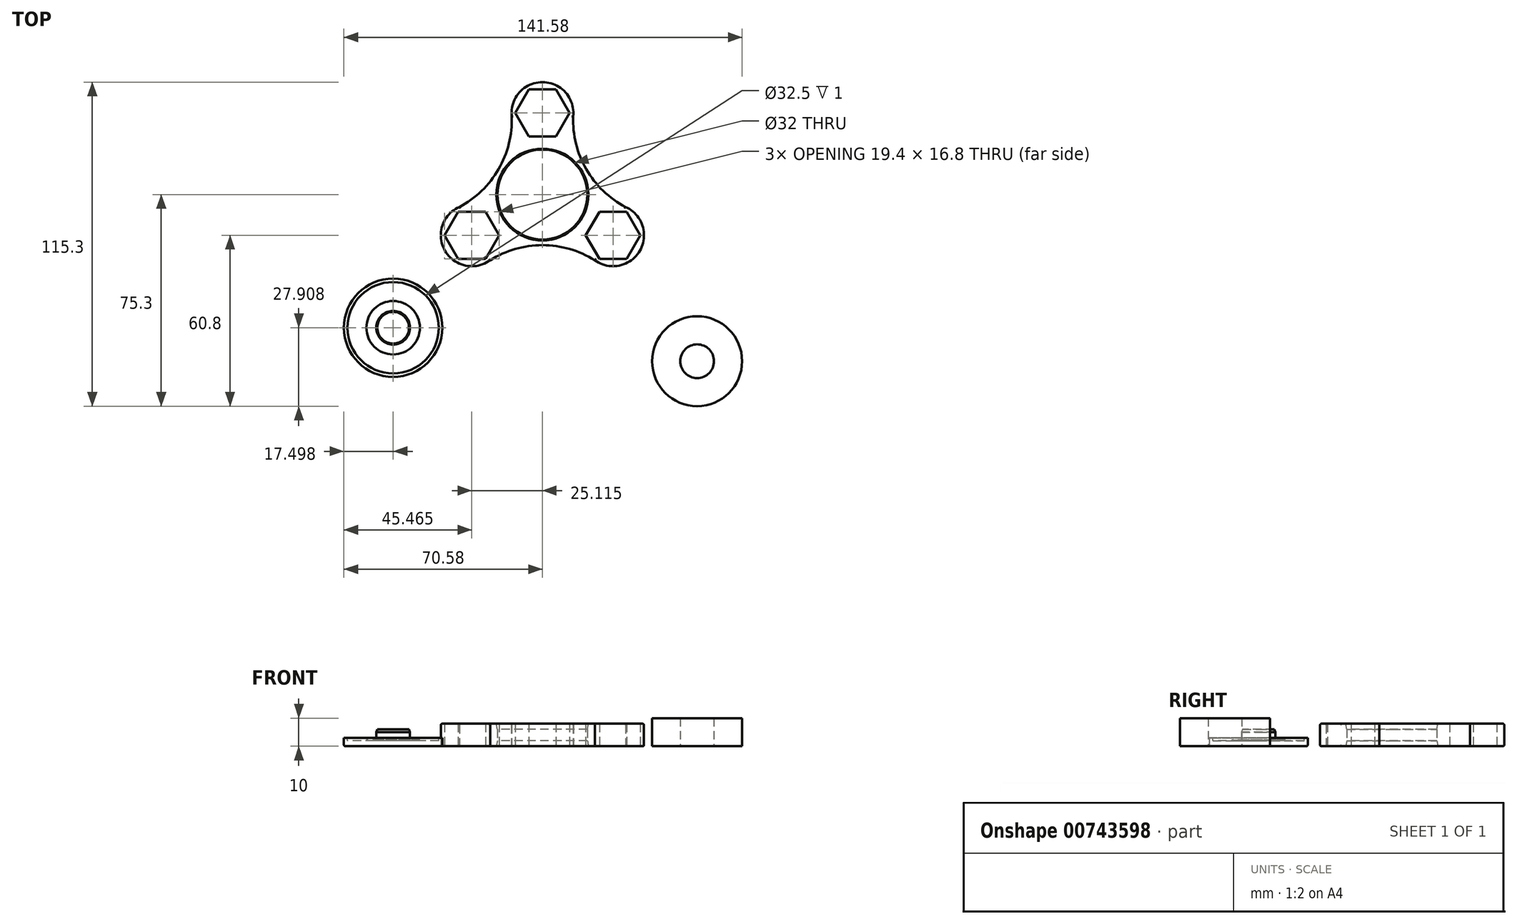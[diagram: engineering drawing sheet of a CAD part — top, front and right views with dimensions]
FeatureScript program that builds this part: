
annotation { "Feature Type Name" : "Feature", "Feature Type Description" : "" }
export const myFeature = defineFeature(function(context is Context, id is Id, definition is map)
    precondition{}
    {
        {
            var Q0;
            Q0=qCreatedBy(makeId("Top.planeOp"),FACE);
            var sketch = newSketch(context, id + "F0", { "sketchPlane" : qUnion([Q0])});
            skCircle(sketch, "E0", {"center": v(0, 0) * mm, "radius": 16 * mm});
            skCircle(sketch, "E1", {"center": v(0, 0) * mm, "radius": 40 * mm, "construction": true});
            skCircle(sketch, "E2.cCircle", {"center": v(0, 29) * mm, "radius": 8.4 * mm, "construction": true});
            skLineSegment(sketch, "E2.0", {"start": v(-4.85, 20.6) * mm, "end": v(-9.7, 29) * mm});
            skLineSegment(sketch, "E2.1", {"start": v(-9.7, 29) * mm, "end": v(-4.85, 37.4) * mm});
            skLineSegment(sketch, "E2.2", {"start": v(-4.85, 37.4) * mm, "end": v(4.85, 37.4) * mm});
            skLineSegment(sketch, "E2.3", {"start": v(4.85, 37.4) * mm, "end": v(9.7, 29) * mm});
            skLineSegment(sketch, "E2.4", {"start": v(9.7, 29) * mm, "end": v(4.85, 20.6) * mm});
            skLineSegment(sketch, "E2.5", {"start": v(4.85, 20.6) * mm, "end": v(-4.85, 20.6) * mm});
            skPoint(sketch, "E2.0.midPoint", {"position": v(-7.27, 24.8) * mm});
            skCircle(sketch, "E3", {"center": v(0, 29) * mm, "radius": 11 * mm});
            skCircle(sketch, "E4.1.0", {"center": v(-25.11, -14.5) * mm, "radius": 11 * mm});
            skLineSegment(sketch, "E4.1.1", {"start": v(-29.96, -6.1) * mm, "end": v(-20.26, -6.1) * mm});
            skPoint(sketch, "E4.1.2", {"position": v(-17.84, -18.7) * mm});
            skLineSegment(sketch, "E4.1.3", {"start": v(-20.26, -22.9) * mm, "end": v(-29.96, -22.9) * mm});
            skLineSegment(sketch, "E4.1.4", {"start": v(-29.96, -22.9) * mm, "end": v(-34.81, -14.5) * mm});
            skLineSegment(sketch, "E4.1.5", {"start": v(-15.42, -14.5) * mm, "end": v(-20.26, -22.9) * mm});
            skCircle(sketch, "E4.1.6", {"center": v(-25.11, -14.5) * mm, "radius": 8.4 * mm, "construction": true});
            skLineSegment(sketch, "E4.1.7", {"start": v(-34.81, -14.5) * mm, "end": v(-29.96, -6.1) * mm});
            skLineSegment(sketch, "E4.1.8", {"start": v(-20.26, -6.1) * mm, "end": v(-15.42, -14.5) * mm});
            skCircle(sketch, "E4.2.0", {"center": v(25.11, -14.5) * mm, "radius": 11 * mm});
            skLineSegment(sketch, "E4.2.1", {"start": v(20.26, -22.9) * mm, "end": v(15.42, -14.5) * mm});
            skPoint(sketch, "E4.2.2", {"position": v(25.11, -6.1) * mm});
            skLineSegment(sketch, "E4.2.3", {"start": v(29.96, -6.1) * mm, "end": v(34.81, -14.5) * mm});
            skLineSegment(sketch, "E4.2.4", {"start": v(34.81, -14.5) * mm, "end": v(29.96, -22.9) * mm});
            skLineSegment(sketch, "E4.2.5", {"start": v(20.26, -6.1) * mm, "end": v(29.96, -6.1) * mm});
            skCircle(sketch, "E4.2.6", {"center": v(25.11, -14.5) * mm, "radius": 8.4 * mm, "construction": true});
            skLineSegment(sketch, "E4.2.7", {"start": v(29.96, -22.9) * mm, "end": v(20.26, -22.9) * mm});
            skLineSegment(sketch, "E4.2.8", {"start": v(15.42, -14.5) * mm, "end": v(20.26, -6.1) * mm});
            skPoint(sketch, "E5.0.internal.snap0", {"position": v(-25.11, -6.1) * mm});
            skLineSegment(sketch, "E6", {"start": v(0, 0) * mm, "end": v(34.64, 20) * mm, "construction": true});
            skLineSegment(sketch, "E7", {"start": v(0, 0) * mm, "end": v(25.11, -14.5) * mm, "construction": true});
            skCircle(sketch, "E8", {"center": v(0, 0) * mm, "radius": 18 * mm});
            skLineSegment(sketch, "E9", {"start": v(0, 29) * mm, "end": v(11, 29) * mm, "construction": true});
            skPoint(sketch, "E10", {"position": v(11, 29) * mm});
            skCircle(sketch, "E11", {"center": v(0, 0) * mm, "radius": 31.02 * mm, "construction": true});
            skArc(sketch, "E12", {"start": v(11, 29) * mm, "mid": v(11.8, 18.66) * mm, "end": v(15.59, 9) * mm});
            skPoint(sketch, "E13.MirrorP", {"position": v(-11, 29) * mm});
            skLineSegment(sketch, "E14.MirrorCS", {"start": v(0, 29) * mm, "end": v(-11, 29) * mm, "construction": true});
            skPoint(sketch, "E15.1.0", {"position": v(-19.61, -24.03) * mm});
            skPoint(sketch, "E15.1.1", {"position": v(-30.61, -4.97) * mm});
            skPoint(sketch, "E15.2.0", {"position": v(30.61, -4.97) * mm});
            skPoint(sketch, "E15.2.1", {"position": v(19.61, -24.03) * mm});
            skLineSegment(sketch, "E16", {"start": v(0, 0) * mm, "end": v(30.61, -4.97) * mm, "construction": true});
            skArc(sketch, "E17", {"start": v(15.59, 9) * mm, "mid": v(22.05, 0.89) * mm, "end": v(30.61, -4.97) * mm});
            skArc(sketch, "E18.1.0", {"start": v(-30.61, -4.97) * mm, "mid": v(-22.05, 0.89) * mm, "end": v(-15.59, 9) * mm});
            skArc(sketch, "E18.1.1", {"start": v(-15.59, 9) * mm, "mid": v(-11.8, 18.66) * mm, "end": v(-11, 29) * mm});
            skArc(sketch, "E18.2.0", {"start": v(19.61, -24.03) * mm, "mid": v(10.26, -19.54) * mm, "end": v(0, -18) * mm});
            skArc(sketch, "E18.2.1", {"start": v(0, -18) * mm, "mid": v(-10.26, -19.54) * mm, "end": v(-19.61, -24.03) * mm});
            skSolve(sketch);
        }
        {
            var Q0;
            Q0 = qSketchRegion(id + "F0", true);
            extrude(context, id + "F1", {"entities" : qUnion([Q0]), "depth" : 8 * mm, "offsetDistance" : 25 * mm});
        }
        {
            var Q0;
            Q0=makeQuery(id+"F1.opExtrude","CAP_EDGE",EDGE,{"disambiguationData":[OSD([sQuery(id+"F0.wireOp",EDGE,"E0")])],"isStart":false});
            var Q1;
            Q1=makeQuery(id+"F1.opExtrude","SWEPT_FACE",FACE,{"disambiguationData":[OSD([sQuery(id+"F0.wireOp",EDGE,"E0")])]});
            chamfer(context, id + "F2", {"entities" : qUnion([Q0, Q1]), "chamferType" : ChamferType.OFFSET_ANGLE, "width" : 2 * mm, "oppositeDirection" : false, "angle" : 10 * degree, "tangentPropagation" : true});
        }
        {
            var Q0;
            Q0=makeQuery(id+"F1.opExtrude","CAP_EDGE",EDGE,{"disambiguationData":[OSD([sQuery(id+"F0.wireOp",EDGE,"E4.2.0")])],"isStart":false});
            var Q1;
            Q1=makeQuery(id+"F1.opExtrude","CAP_EDGE",EDGE,{"disambiguationData":[OSD([sQuery(id+"F0.wireOp",EDGE,"E4.1.0")])],"isStart":false});
            var Q2;
            Q2=makeQuery(id+"F1.opExtrude","CAP_EDGE",EDGE,{"disambiguationData":[OSD([sQuery(id+"F0.wireOp",EDGE,"E3")])],"isStart":false});
            var Q3;
            Q3=makeQuery(id+"F1.opExtrude","CAP_EDGE",EDGE,{"disambiguationData":[OSD([sQuery(id+"F0.wireOp",EDGE,"E12")])],"isStart":true});
            var Q4;
            Q4=makeQuery(id+"F1.opExtrude","CAP_EDGE",EDGE,{"disambiguationData":[OSD([sQuery(id+"F0.wireOp",EDGE,"E18.2.0")])],"isStart":true});
            var Q5;
            Q5=makeQuery(id+"F1.opExtrude","CAP_EDGE",EDGE,{"disambiguationData":[OSD([sQuery(id+"F0.wireOp",EDGE,"E18.1.0")])],"isStart":true});
            var Q6;
            Q6=makeQuery(id+"F1.opExtrude","CAP_EDGE",EDGE,{"disambiguationData":[OSD([sQuery(id+"F0.wireOp",EDGE,"E4.2.0")])],"isStart":true});
            var Q7;
            Q7=makeQuery(id+"F1.opExtrude","CAP_EDGE",EDGE,{"disambiguationData":[OSD([sQuery(id+"F0.wireOp",EDGE,"E3")])],"isStart":true});
            var Q8;
            Q8=makeQuery(id+"F1.opExtrude","CAP_EDGE",EDGE,{"disambiguationData":[OSD([sQuery(id+"F0.wireOp",EDGE,"E18.1.1")])],"isStart":true});
            var Q9;
            Q9=makeQuery(id+"F1.opExtrude","CAP_EDGE",EDGE,{"disambiguationData":[OSD([sQuery(id+"F0.wireOp",EDGE,"E17")])],"isStart":true});
            var Q10;
            Q10=makeQuery(id+"F1.opExtrude","CAP_EDGE",EDGE,{"disambiguationData":[OSD([sQuery(id+"F0.wireOp",EDGE,"E4.1.0")])],"isStart":true});
            var Q11;
            Q11=makeQuery(id+"F1.opExtrude","CAP_EDGE",EDGE,{"disambiguationData":[OSD([sQuery(id+"F0.wireOp",EDGE,"E18.2.1")])],"isStart":true});
            var Q12;
            Q12=makeQuery(id+"F1.opExtrude","CAP_EDGE",EDGE,{"disambiguationData":[OSD([sQuery(id+"F0.wireOp",EDGE,"E12")])],"isStart":false});
            var Q13;
            Q13=makeQuery(id+"F1.opExtrude","CAP_EDGE",EDGE,{"disambiguationData":[OSD([sQuery(id+"F0.wireOp",EDGE,"E17")])],"isStart":false});
            var Q14;
            Q14=makeQuery(id+"F1.opExtrude","CAP_EDGE",EDGE,{"disambiguationData":[OSD([sQuery(id+"F0.wireOp",EDGE,"E18.2.1")])],"isStart":false});
            var Q15;
            Q15=makeQuery(id+"F1.opExtrude","CAP_EDGE",EDGE,{"disambiguationData":[OSD([sQuery(id+"F0.wireOp",EDGE,"E18.2.0")])],"isStart":false});
            var Q16;
            Q16=makeQuery(id+"F1.opExtrude","CAP_EDGE",EDGE,{"disambiguationData":[OSD([sQuery(id+"F0.wireOp",EDGE,"E18.1.0")])],"isStart":false});
            var Q17;
            Q17=makeQuery(id+"F1.opExtrude","CAP_EDGE",EDGE,{"disambiguationData":[OSD([sQuery(id+"F0.wireOp",EDGE,"E18.1.1")])],"isStart":false});
            fillet(context, id + "F3", {"entities" : qUnion([Q0, Q1, Q2, Q3, Q4, Q5, Q6, Q7, Q8, Q9, Q10, Q11, Q12, Q13, Q14, Q15, Q16, Q17]), "radius" : 0.5 * mm, "tangentPropagation" : true, "allowEdgeOverflow" : false});
        }
        {
            var Q0;
            Q0=qCreatedBy(makeId("Top.planeOp"),FACE);
            var sketch = newSketch(context, id + "F4", { "sketchPlane" : qUnion([Q0])});
            skCircle(sketch, "E19", {"center": v(-53.08, -47.4) * mm, "radius": 17.5 * mm});
            skSolve(sketch);
        }
        {
            var Q0;
            Q0=makeQuery(id+"F4.imprint","IMPRINT",FACE,{"disambiguationData":[TD([[makeQuery(id+"F4.imprint","IMPRINT",EDGE,{"derivedFrom":sQuery(id+"F4.wireOp",EDGE,"E19")}),1.0]])]});
            extrude(context, id + "F5", {"entities" : qUnion([Q0]), "depth" : 3 * mm, "offsetDistance" : 25 * mm});
        }
        {
            var Q0;
            Q0=makeQuery(id+"F5.opExtrude","CAP_FACE",FACE,{"disambiguationData":[OSD([sQuery(id+"F4.wireOp",EDGE,"E19")])],"isStart":false});
            var sketch = newSketch(context, id + "F6", { "sketchPlane" : qUnion([Q0])});
            skCircle(sketch, "E20", {"center": v(-53.08, -47.4) * mm, "radius": 16.25 * mm});
            skSolve(sketch);
        }
        {
            var Q0;
            Q0=makeQuery(id+"F6.imprint","IMPRINT",FACE,{"disambiguationData":[TD([[makeQuery(id+"F6.imprint","IMPRINT",EDGE,{"derivedFrom":sQuery(id+"F6.wireOp",EDGE,"E20")}),1.0]])]});
            extrude(context, id + "F7", {"entities" : qUnion([Q0]), "operationType" : NewBodyOperationType.REMOVE, "oppositeDirection" : true, "depth" : 1 * mm, "offsetDistance" : 25 * mm});
        }
        {
            var Q0;
            Q0=makeQuery(id+"F7.boolean.opBoolean","COPY",FACE,{"derivedFrom":makeQuery(id+"F7.opExtrude","CAP_FACE",FACE,{"disambiguationData":[OSD([sQuery(id+"F6.wireOp",EDGE,"E20")])],"isStart":false})});
            var sketch = newSketch(context, id + "F8", { "sketchPlane" : qUnion([Q0])});
            skCircle(sketch, "E21", {"center": v(-53.08, -47.4) * mm, "radius": 6 * mm});
            skSolve(sketch);
        }
        {
            var Q0;
            Q0 = qSketchRegion(id + "F8", true);
            extrude(context, id + "F9", {"entities" : qUnion([Q0]), "operationType" : NewBodyOperationType.ADD, "depth" : 4 * mm, "offsetDistance" : 25 * mm});
        }
        {
            var Q0;
            Q0=makeQuery(id+"F9.opExtrude","CAP_EDGE",EDGE,{"disambiguationData":[OSD([sQuery(id+"F8.wireOp",EDGE,"E21")])],"isStart":false});
            chamfer(context, id + "F10", {"entities" : qUnion([Q0]), "chamferType" : ChamferType.OFFSET_ANGLE, "width" : 1 * mm, "oppositeDirection" : true, "angle" : 20 * degree, "tangentPropagation" : true});
        }
        {
            var Q0;
            Q0=qCreatedBy(makeId("Top.planeOp"),FACE);
            var sketch = newSketch(context, id + "F11", { "sketchPlane" : qUnion([Q0])});
            skCircle(sketch, "E22", {"center": v(55, -59.3) * mm, "radius": 16 * mm});
            skCircle(sketch, "E23", {"center": v(55, -59.3) * mm, "radius": 6 * mm});
            skSolve(sketch);
        }
        {
            var Q0;
            Q0 = qSketchRegion(id + "F11", true);
            extrude(context, id + "F12", {"entities" : qUnion([Q0]), "depth" : 10 * mm, "offsetDistance" : 25 * mm});
        }
        {
            var Q0;
            Q0=makeQuery(id+"F7.boolean.opBoolean","COPY",FACE,{"derivedFrom":makeQuery(id+"F7.opExtrude","CAP_FACE",FACE,{"disambiguationData":[OSD([sQuery(id+"F6.wireOp",EDGE,"E20")])],"isStart":false})});
            var sketch = newSketch(context, id + "F13", { "sketchPlane" : qUnion([Q0])});
            skCircle(sketch, "E24", {"center": v(-53.08, -47.4) * mm, "radius": 9.5 * mm});
            skSolve(sketch);
        }
        {
            var Q0;
            Q0=makeQuery(id+"F13.imprint","IMPRINT",FACE,{"disambiguationData":[TD([[makeQuery(id+"F13.imprint","IMPRINT",EDGE,{"derivedFrom":sQuery(id+"F13.wireOp",EDGE,"E24")}),1.0]])]});
            extrude(context, id + "F14", {"entities" : qUnion([Q0]), "operationType" : NewBodyOperationType.ADD, "depth" : 0.2 * mm, "offsetDistance" : 25 * mm});
        }
        {
            var Q0;
            Q0=makeQuery(id+"F5.opExtrude","CAP_EDGE",EDGE,{"disambiguationData":[OSD([sQuery(id+"F4.wireOp",EDGE,"E19")])],"isStart":true});
            fillet(context, id + "F15", {"entities" : qUnion([Q0]), "radius" : 0.5 * mm, "tangentPropagation" : true, "allowEdgeOverflow" : false});
        }
    });
